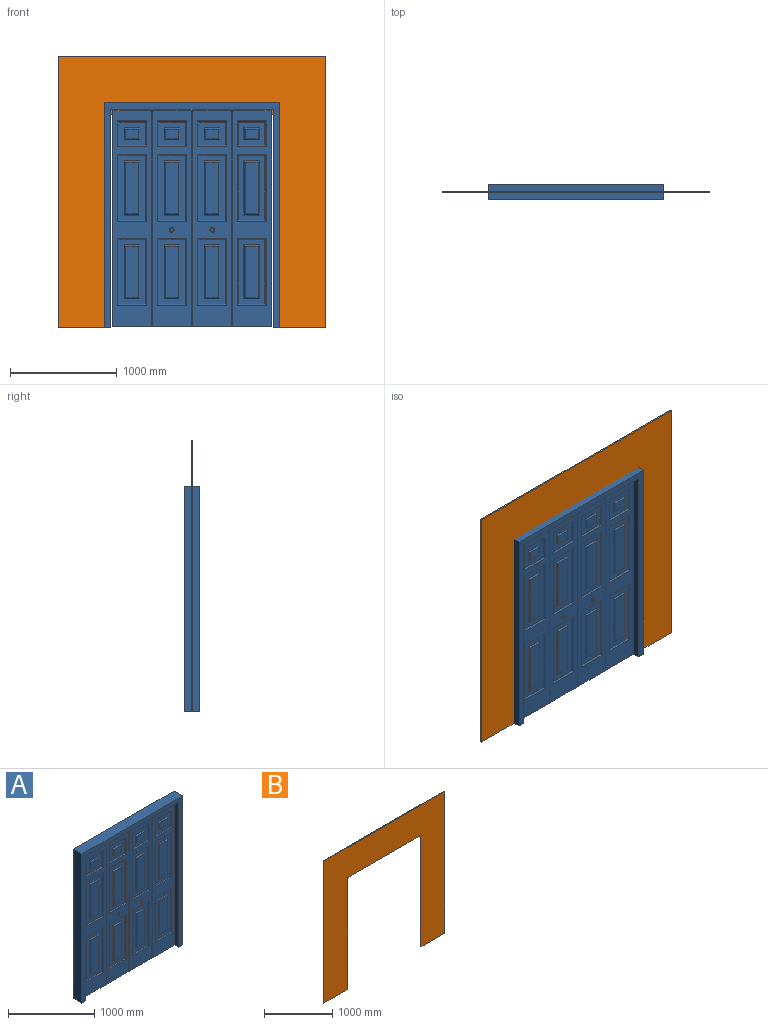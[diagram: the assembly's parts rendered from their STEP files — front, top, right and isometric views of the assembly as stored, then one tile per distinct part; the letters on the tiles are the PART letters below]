
ASSEMBLY  parts=2 mates=1
PART A: 174 faces, bbox 1651x139.7x2114.6 mm
  f0: plane 2038.35x369.89mm, normal (0,-1,0), area 336636.8mm2, adj f13,f22,f23,f24,f25,f36,f37,f45
  f1: plane 2038.35x369.89mm, normal (0,-1,0), area 336636.8mm2, adj f13,f26,f27,f28,f29,f39,f40,f43
  f2: plane 2038.35x373.06mm, normal (0,-1,0), area 343194.9mm2, adj f5,f7,f13,f30,f31,f32,f41,f42
  f3: plane 2038.35x373.06mm, normal (0,-1,0), area 343194.9mm2, adj f4,f6,f13,f33,f34,f35,f38,f44
  f4: plane 373.06x38.1mm, normal (0,0,-1), area 14213.7mm2, adj f3,f12,f35,f44
  f5: plane 373.06x38.1mm, normal (0,0,-1), area 14213.7mm2, adj f2,f10,f30,f42
  f6: plane 294.91x38.1mm, normal (0,0,1), area 11236.2mm2, adj f3,f12,f38,f44
  f7: plane 294.91x38.1mm, normal (0,0,1), area 11236.2mm2, adj f2,f10,f41,f42
  f8: plane 2038.35x369.89mm, normal (0,1,0), area 749423.9mm2, adj f13,f22,f23,f24,f25,f36,f37,f45
  f9: plane 2038.35x369.89mm, normal (0,1,0), area 749423.9mm2, adj f13,f26,f27,f28,f29,f39,f40,f43
  f10: plane 2038.35x373.06mm, normal (0,1,0), area 755855.3mm2, adj f5,f7,f13,f30,f31,f32,f41,f42
  f11: plane 139.7x63.5mm, normal (0,0,-1), area 8871mm2, adj f14,f15,f20,f21
  f12: plane 2038.35x373.06mm, normal (0,1,0), area 755855.3mm2, adj f4,f6,f13,f33,f34,f35,f38,f44
  f13: plane 1524x139.7mm, normal (0,0,-1), area 210967.3mm2, adj f0,f1,f2,f3,f8,f9,f10,f12
  f14: plane 2051.05x139.7mm, normal (-1,0,0), area 286531.7mm2, adj f11,f13,f20,f21
  f15: plane 2114.55x139.7mm, normal (1,0,0), area 295402.6mm2, adj f11,f16,f20,f21
  f16: plane 1651x139.7mm, normal (0,0,1), area 230644.7mm2, adj f15,f17,f20,f21
  f17: plane 2114.55x139.7mm, normal (-1,0,0), area 295402.6mm2, adj f16,f18,f20,f21
  f18: plane 139.7x63.5mm, normal (0,0,-1), area 8870.9mm2, adj f17,f19,f20,f21
  f19: plane 2051.05x139.7mm, normal (1,0,0), area 286531.7mm2, adj f13,f18,f20,f21
  f20: plane 2114.55x1651mm, normal (0,-1,0), area 365321.9mm2, adj f11,f13,f14,f15,f16,f17,f18,f19
  f21: plane 2114.55x1651mm, normal (0,1,0), area 365321.9mm2, adj f11,f13,f14,f15,f16,f17,f18,f19
  f22: plane 369.89x38.1mm, normal (0,0,-1), area 14092.7mm2, adj f0,f8,f23,f45
  f23: plane 2025.65x38.1mm, normal (-1,0,0), area 77177.3mm2, adj f0,f8,f22,f24
  f24: plane 134.3x38.1mm, normal (0,0,1), area 5116.9mm2, adj f0,f8,f23,f25
  f25: plane 38.1x12.7mm, normal (-1,0,0), area 483.9mm2, adj f0,f8,f13,f24
  f26: plane 38.1x12.7mm, normal (1,0,0), area 483.9mm2, adj f1,f9,f13,f27
  f27: plane 134.3x38.1mm, normal (0,0,1), area 5116.9mm2, adj f1,f9,f26,f28
  f28: plane 2025.65x38.1mm, normal (1,0,0), area 77177.3mm2, adj f1,f9,f27,f29
  f29: plane 369.89x38.1mm, normal (0,0,-1), area 14092.7mm2, adj f1,f9,f28,f43
  f30: plane 2025.65x38.1mm, normal (-1,0,0), area 77177.3mm2, adj f2,f5,f10,f31
  f31: plane 65.45x38.1mm, normal (0,0,1), area 2493.7mm2, adj f2,f10,f30,f32
  f32: plane 38.1x12.7mm, normal (-1,0,0), area 483.9mm2, adj f2,f10,f13,f31
  f33: plane 38.1x12.7mm, normal (1,0,0), area 483.9mm2, adj f3,f12,f13,f34
  f34: plane 65.45x38.1mm, normal (0,0,1), area 2493.7mm2, adj f3,f12,f33,f35
  f35: plane 2025.65x38.1mm, normal (1,0,0), area 77177.3mm2, adj f3,f4,f12,f34
  f36: plane 38.1x12.7mm, normal (1,0,0), area 483.9mm2, adj f0,f8,f13,f37
  f37: plane 222.89x38.1mm, normal (0,0,1), area 8491.9mm2, adj f0,f8,f36,f45
  f38: plane 38.1x12.7mm, normal (-1,0,0), area 483.9mm2, adj f3,f6,f12,f13
  f39: plane 222.89x38.1mm, normal (0,0,1), area 8491.9mm2, adj f1,f9,f40,f43
  f40: plane 38.1x12.7mm, normal (-1,0,0), area 483.9mm2, adj f1,f9,f13,f39
  f41: plane 38.1x12.7mm, normal (1,0,0), area 483.9mm2, adj f2,f7,f10,f13
  f42: plane 2025.65x38.1mm, normal (1,0,0), area 77177.3mm2, adj f2,f5,f7,f10
  f43: plane 2025.65x38.1mm, normal (-1,0,0), area 77177.3mm2, adj f1,f9,f29,f39
  f44: plane 2025.65x38.1mm, normal (-1,0,0), area 77177.3mm2, adj f3,f4,f6,f12
  f45: plane 2025.65x38.1mm, normal (1,0,0), area 77177.3mm2, adj f0,f8,f22,f37
  f46: plane 609.6x247.65mm, normal (0,-1,0), area 76774mm2, adj f82,f83,f84,f85,f154,f155,f156,f157
  f47: plane 482.6x120.65mm, normal (0,-1,0), area 58225.7mm2, adj f82,f83,f84,f85
  f48: plane 609.6x247.65mm, normal (0,-1,0), area 76774mm2, adj f78,f79,f80,f81,f158,f159,f160,f161
  f49: plane 247.65x215.9mm, normal (0,-1,0), area 36774.1mm2, adj f74,f75,f76,f77,f162,f163,f164,f165
  f50: plane 247.65x215.9mm, normal (0,-1,0), area 36774.1mm2, adj f102,f103,f104,f105,f118,f119,f120,f121
  f51: plane 120.65x88.9mm, normal (0,-1,0), area 10725.8mm2, adj f102,f103,f104,f105
  f52: plane 609.6x247.65mm, normal (0,-1,0), area 76774mm2, adj f98,f99,f100,f101,f142,f143,f144,f145
  f53: plane 609.6x247.65mm, normal (0,-1,0), area 76774mm2, adj f114,f115,f116,f117,f138,f139,f140,f141
  f54: plane 482.6x120.65mm, normal (0,-1,0), area 58225.7mm2, adj f114,f115,f116,f117
  f55: plane 247.65x215.9mm, normal (0,-1,0), area 36774.1mm2, adj f106,f107,f108,f109,f122,f123,f124,f125
  f56: plane 609.6x247.65mm, normal (0,-1,0), area 76774mm2, adj f110,f111,f112,f113,f134,f135,f136,f137
  f57: plane 609.6x247.65mm, normal (0,-1,0), area 76774mm2, adj f94,f95,f96,f97,f146,f147,f148,f149
  f58: plane 482.6x120.65mm, normal (0,-1,0), area 58225.7mm2, adj f94,f95,f96,f97
  f59: plane 609.6x247.65mm, normal (0,-1,0), area 76774mm2, adj f90,f91,f92,f93,f150,f151,f152,f153
  f60: plane 609.6x247.65mm, normal (0,-1,0), area 76774mm2, adj f86,f87,f88,f89,f130,f131,f132,f133
  f61: plane 482.6x120.65mm, normal (0,-1,0), area 58225.7mm2, adj f86,f87,f88,f89
  f62: plane 247.65x215.9mm, normal (0,-1,0), area 36774.1mm2, adj f70,f71,f72,f73,f126,f127,f128,f129
  f63: plane 120.65x88.9mm, normal (0,-1,0), area 10725.8mm2, adj f70,f71,f72,f73
  f64: plane 482.6x120.65mm, normal (0,-1,0), area 58225.7mm2, adj f78,f79,f80,f81
  f65: plane 120.65x88.9mm, normal (0,-1,0), area 10725.8mm2, adj f74,f75,f76,f77
  f66: plane 482.6x120.65mm, normal (0,-1,0), area 58225.7mm2, adj f98,f99,f100,f101
  f67: plane 120.65x88.9mm, normal (0,-1,0), area 10725.8mm2, adj f106,f107,f108,f109
  f68: plane 482.6x120.65mm, normal (0,-1,0), area 58225.7mm2, adj f110,f111,f112,f113
  f69: plane 482.6x120.65mm, normal (0,-1,0), area 58225.7mm2, adj f90,f91,f92,f93
  f70: plane 146.05x12.7mm, normal (0,-0.71,0.71), area 2395mm2, adj f62,f63,f71,f72
  f71: plane 114.3x12.7mm, normal (-0.71,-0.71,0), area 1824.8mm2, adj f62,f63,f70,f73
  f72: plane 114.3x12.7mm, normal (0.71,-0.71,0), area 1824.8mm2, adj f62,f63,f70,f73
  f73: plane 146.05x12.7mm, normal (0,-0.71,-0.71), area 2395mm2, adj f62,f63,f71,f72
  f74: plane 146.05x12.7mm, normal (0,-0.71,0.71), area 2395mm2, adj f49,f65,f75,f76
  f75: plane 114.3x12.7mm, normal (0.71,-0.71,0), area 1824.8mm2, adj f49,f65,f74,f77
  f76: plane 114.3x12.7mm, normal (-0.71,-0.71,0), area 1824.8mm2, adj f49,f65,f74,f77
  f77: plane 146.05x12.7mm, normal (0,-0.71,-0.71), area 2395mm2, adj f49,f65,f75,f76
  f78: plane 146.05x12.7mm, normal (0,-0.71,-0.71), area 2395mm2, adj f48,f64,f79,f80
  f79: plane 508x12.7mm, normal (0.71,-0.71,0), area 8895.8mm2, adj f48,f64,f78,f81
  f80: plane 508x12.7mm, normal (-0.71,-0.71,0), area 8895.8mm2, adj f48,f64,f78,f81
  f81: plane 146.05x12.7mm, normal (0,-0.71,0.71), area 2395mm2, adj f48,f64,f79,f80
  f82: plane 508x12.7mm, normal (-0.71,-0.71,0), area 8895.8mm2, adj f46,f47,f83,f84
  f83: plane 146.05x12.7mm, normal (0,-0.71,0.71), area 2395mm2, adj f46,f47,f82,f85
  f84: plane 146.05x12.7mm, normal (0,-0.71,-0.71), area 2395mm2, adj f46,f47,f82,f85
  f85: plane 508x12.7mm, normal (0.71,-0.71,0), area 8895.8mm2, adj f46,f47,f83,f84
  f86: plane 146.05x12.7mm, normal (0,-0.71,0.71), area 2395mm2, adj f60,f61,f87,f88
  f87: plane 508x12.7mm, normal (-0.71,-0.71,0), area 8895.8mm2, adj f60,f61,f86,f89
  f88: plane 508x12.7mm, normal (0.71,-0.71,0), area 8895.8mm2, adj f60,f61,f86,f89
  f89: plane 146.05x12.7mm, normal (0,-0.71,-0.71), area 2395mm2, adj f60,f61,f87,f88
  f90: plane 146.05x12.7mm, normal (0,-0.71,0.71), area 2395mm2, adj f59,f69,f91,f92
  f91: plane 508x12.7mm, normal (0.71,-0.71,0), area 8895.8mm2, adj f59,f69,f90,f93
  f92: plane 508x12.7mm, normal (-0.71,-0.71,0), area 8895.8mm2, adj f59,f69,f90,f93
  f93: plane 146.05x12.7mm, normal (0,-0.71,-0.71), area 2395mm2, adj f59,f69,f91,f92
  f94: plane 508x12.7mm, normal (-0.71,-0.71,0), area 8895.8mm2, adj f57,f58,f95,f96
  f95: plane 146.05x12.7mm, normal (0,-0.71,0.71), area 2395mm2, adj f57,f58,f94,f97
  f96: plane 146.05x12.7mm, normal (0,-0.71,-0.71), area 2395mm2, adj f57,f58,f94,f97
  f97: plane 508x12.7mm, normal (0.71,-0.71,0), area 8895.8mm2, adj f57,f58,f95,f96
  f98: plane 146.05x12.7mm, normal (0,-0.71,0.71), area 2395mm2, adj f52,f66,f99,f100
  f99: plane 508x12.7mm, normal (0.71,-0.71,0), area 8895.8mm2, adj f52,f66,f98,f101
  f100: plane 508x12.7mm, normal (-0.71,-0.71,0), area 8895.8mm2, adj f52,f66,f98,f101
  f101: plane 146.05x12.7mm, normal (0,-0.71,-0.71), area 2395mm2, adj f52,f66,f99,f100
  f102: plane 146.05x12.7mm, normal (0,-0.71,0.71), area 2395mm2, adj f50,f51,f103,f104
  f103: plane 114.3x12.7mm, normal (-0.71,-0.71,0), area 1824.8mm2, adj f50,f51,f102,f105
  f104: plane 114.3x12.7mm, normal (0.71,-0.71,0), area 1824.8mm2, adj f50,f51,f102,f105
  f105: plane 146.05x12.7mm, normal (0,-0.71,-0.71), area 2395mm2, adj f50,f51,f103,f104
  f106: plane 146.05x12.7mm, normal (0,-0.71,0.71), area 2395mm2, adj f55,f67,f107,f108
  f107: plane 114.3x12.7mm, normal (0.71,-0.71,0), area 1824.8mm2, adj f55,f67,f106,f109
  f108: plane 114.3x12.7mm, normal (-0.71,-0.71,0), area 1824.8mm2, adj f55,f67,f106,f109
  f109: plane 146.05x12.7mm, normal (0,-0.71,-0.71), area 2395mm2, adj f55,f67,f107,f108
  f110: plane 146.05x12.7mm, normal (0,-0.71,-0.71), area 2395mm2, adj f56,f68,f111,f112
  f111: plane 508x12.7mm, normal (0.71,-0.71,0), area 8895.8mm2, adj f56,f68,f110,f113
  f112: plane 508x12.7mm, normal (-0.71,-0.71,0), area 8895.8mm2, adj f56,f68,f110,f113
  f113: plane 146.05x12.7mm, normal (0,-0.71,0.71), area 2395mm2, adj f56,f68,f111,f112
  f114: plane 146.05x12.7mm, normal (0,-0.71,0.71), area 2395mm2, adj f53,f54,f115,f116
  f115: plane 508x12.7mm, normal (-0.71,-0.71,0), area 8895.8mm2, adj f53,f54,f114,f117
  f116: plane 508x12.7mm, normal (0.71,-0.71,0), area 8895.8mm2, adj f53,f54,f114,f117
  f117: plane 146.05x12.7mm, normal (0,-0.71,-0.71), area 2395mm2, adj f53,f54,f115,f116
  f118: plane 273.05x12.7mm, normal (0,-0.71,0.71), area 4676mm2, adj f2,f50,f119,f120
  f119: plane 241.3x12.7mm, normal (0.71,-0.71,0), area 4105.8mm2, adj f2,f50,f118,f121
  f120: plane 241.3x12.7mm, normal (-0.71,-0.71,0), area 4105.8mm2, adj f2,f50,f118,f121
  f121: plane 273.05x12.7mm, normal (0,-0.71,-0.71), area 4676mm2, adj f2,f50,f119,f120
  f122: plane 273.05x12.7mm, normal (0,-0.71,0.71), area 4676mm2, adj f1,f55,f123,f124
  f123: plane 241.3x12.7mm, normal (-0.71,-0.71,0), area 4105.8mm2, adj f1,f55,f122,f125
  f124: plane 241.3x12.7mm, normal (0.71,-0.71,0), area 4105.8mm2, adj f1,f55,f122,f125
  f125: plane 273.05x12.7mm, normal (0,-0.71,-0.71), area 4676mm2, adj f1,f55,f123,f124
  f126: plane 241.3x12.7mm, normal (0.71,-0.71,0), area 4105.8mm2, adj f0,f62,f127,f128
  f127: plane 273.05x12.7mm, normal (0,-0.71,-0.71), area 4676mm2, adj f0,f62,f126,f129
  f128: plane 273.05x12.7mm, normal (0,-0.71,0.71), area 4676mm2, adj f0,f62,f126,f129
  f129: plane 241.3x12.7mm, normal (-0.71,-0.71,0), area 4105.8mm2, adj f0,f62,f127,f128
  f130: plane 273.05x12.7mm, normal (0,-0.71,0.71), area 4676mm2, adj f0,f60,f131,f132
  f131: plane 635x12.7mm, normal (0.71,-0.71,0), area 11176.8mm2, adj f0,f60,f130,f133
  f132: plane 635x12.7mm, normal (-0.71,-0.71,0), area 11176.8mm2, adj f0,f60,f130,f133
  f133: plane 273.05x12.7mm, normal (0,-0.71,-0.71), area 4676mm2, adj f0,f60,f131,f132
  f134: plane 273.05x12.7mm, normal (0,-0.71,-0.71), area 4676mm2, adj f1,f56,f135,f136
  f135: plane 635x12.7mm, normal (-0.71,-0.71,0), area 11176.8mm2, adj f1,f56,f134,f137
  f136: plane 635x12.7mm, normal (0.71,-0.71,0), area 11176.8mm2, adj f1,f56,f134,f137
  f137: plane 273.05x12.7mm, normal (0,-0.71,0.71), area 4676mm2, adj f1,f56,f135,f136
  f138: plane 273.05x12.7mm, normal (0,-0.71,0.71), area 4676mm2, adj f2,f53,f139,f140
  f139: plane 635x12.7mm, normal (0.71,-0.71,0), area 11176.8mm2, adj f2,f53,f138,f141
  f140: plane 635x12.7mm, normal (-0.71,-0.71,0), area 11176.8mm2, adj f2,f53,f138,f141
  f141: plane 273.05x12.7mm, normal (0,-0.71,-0.71), area 4676mm2, adj f2,f53,f139,f140
  f142: plane 273.05x12.7mm, normal (0,-0.71,0.71), area 4676mm2, adj f2,f52,f143,f144
  f143: plane 635x12.7mm, normal (-0.71,-0.71,0), area 11176.8mm2, adj f2,f52,f142,f145
  f144: plane 635x12.7mm, normal (0.71,-0.71,0), area 11176.8mm2, adj f2,f52,f142,f145
  f145: plane 273.05x12.7mm, normal (0,-0.71,-0.71), area 4676mm2, adj f2,f52,f143,f144
  f146: plane 273.05x12.7mm, normal (0,-0.71,-0.71), area 4676mm2, adj f1,f57,f147,f148
  f147: plane 635x12.7mm, normal (0.71,-0.71,0), area 11176.8mm2, adj f1,f57,f146,f149
  f148: plane 635x12.7mm, normal (-0.71,-0.71,0), area 11176.8mm2, adj f1,f57,f146,f149
  f149: plane 273.05x12.7mm, normal (0,-0.71,0.71), area 4676mm2, adj f1,f57,f147,f148
  f150: plane 273.05x12.7mm, normal (0,-0.71,0.71), area 4676mm2, adj f0,f59,f151,f152
  f151: plane 635x12.7mm, normal (-0.71,-0.71,0), area 11176.8mm2, adj f0,f59,f150,f153
  f152: plane 635x12.7mm, normal (0.71,-0.71,0), area 11176.8mm2, adj f0,f59,f150,f153
  f153: plane 273.05x12.7mm, normal (0,-0.71,-0.71), area 4676mm2, adj f0,f59,f151,f152
  f154: plane 273.05x12.7mm, normal (0,-0.71,-0.71), area 4676mm2, adj f3,f46,f155,f156
  f155: plane 635x12.7mm, normal (0.71,-0.71,0), area 11176.8mm2, adj f3,f46,f154,f157
  f156: plane 635x12.7mm, normal (-0.71,-0.71,0), area 11176.8mm2, adj f3,f46,f154,f157
  f157: plane 273.05x12.7mm, normal (0,-0.71,0.71), area 4676mm2, adj f3,f46,f155,f156
  f158: plane 273.05x12.7mm, normal (0,-0.71,-0.71), area 4676mm2, adj f3,f48,f159,f160
  f159: plane 635x12.7mm, normal (-0.71,-0.71,0), area 11176.8mm2, adj f3,f48,f158,f161
  f160: plane 635x12.7mm, normal (0.71,-0.71,0), area 11176.8mm2, adj f3,f48,f158,f161
  f161: plane 273.05x12.7mm, normal (0,-0.71,0.71), area 4676mm2, adj f3,f48,f159,f160
  f162: plane 241.3x12.7mm, normal (0.71,-0.71,0), area 4105.8mm2, adj f3,f49,f163,f164
  f163: plane 273.05x12.7mm, normal (0,-0.71,-0.71), area 4676mm2, adj f3,f49,f162,f165
  f164: plane 273.05x12.7mm, normal (0,-0.71,0.71), area 4676mm2, adj f3,f49,f162,f165
  f165: plane 241.3x12.7mm, normal (-0.71,-0.71,0), area 4105.8mm2, adj f3,f49,f163,f164
  f166: cylinder r=6.35mm len=12.7mm, axis (0,1,0), area 506.7mm2, adj f1,f168
  f167: plane 35.03x35.03mm, normal (0,-1,0), area 963.8mm2, adj f173
  f168: plane 44.45x44.45mm, normal (0,1,0), area 1425.1mm2, adj f166,f173
  f169: cylinder r=6.35mm len=12.7mm, axis (0,1,0), area 506.7mm2, adj f0,f171
  f170: plane 35.03x35.03mm, normal (0,-1,0), area 963.8mm2, adj f172
  f171: plane 44.45x44.45mm, normal (0,1,0), area 1425.1mm2, adj f169,f172
  f172: torus R=17.52mm, axis (0,1,0), area 764.6mm2, adj f170,f171
  f173: torus R=17.52mm, axis (0,1,0), area 764.6mm2, adj f167,f168
PART B: 10 faces, bbox 2514.6x12.7x2552.7 mm
  f0: plane 495.3x12.7mm, normal (0,0,-1), area 6290.3mm2, adj f4,f5,f6,f7
  f1: plane 2514.6x12.7mm, normal (0,0,1), area 31935.4mm2, adj f2,f4,f5,f6
  f2: plane 2552.7x12.7mm, normal (-1,0,0), area 32419.3mm2, adj f1,f3,f5,f6
  f3: plane 495.3x12.7mm, normal (0,0,-1), area 6290.3mm2, adj f2,f5,f6,f9
  f4: plane 2552.7x12.7mm, normal (1,0,0), area 32419.3mm2, adj f0,f1,f5,f6
  f5: plane 2552.7x2514.6mm, normal (0,-1,0), area 3360961mm2, adj f0,f1,f2,f3,f4,f7,f8,f9
  f6: plane 2552.7x2514.6mm, normal (0,1,0), area 3360961mm2, adj f0,f1,f2,f3,f4,f7,f8,f9
  f7: plane 2006.6x12.7mm, normal (-1,0,0), area 25483.8mm2, adj f0,f5,f6,f8
  f8: plane 1524x12.7mm, normal (0,0,-1), area 19354.8mm2, adj f5,f6,f7,f9
  f9: plane 2006.6x12.7mm, normal (1,0,0), area 25483.8mm2, adj f3,f5,f6,f8
PLACE A t=(0,-6.35,-219.07)mm
PLACE B at identity fixed
MATE fastened B.f7 <-> A.f14  axis (-1,0,0) through (762,-6.35,-1276.35)mm
